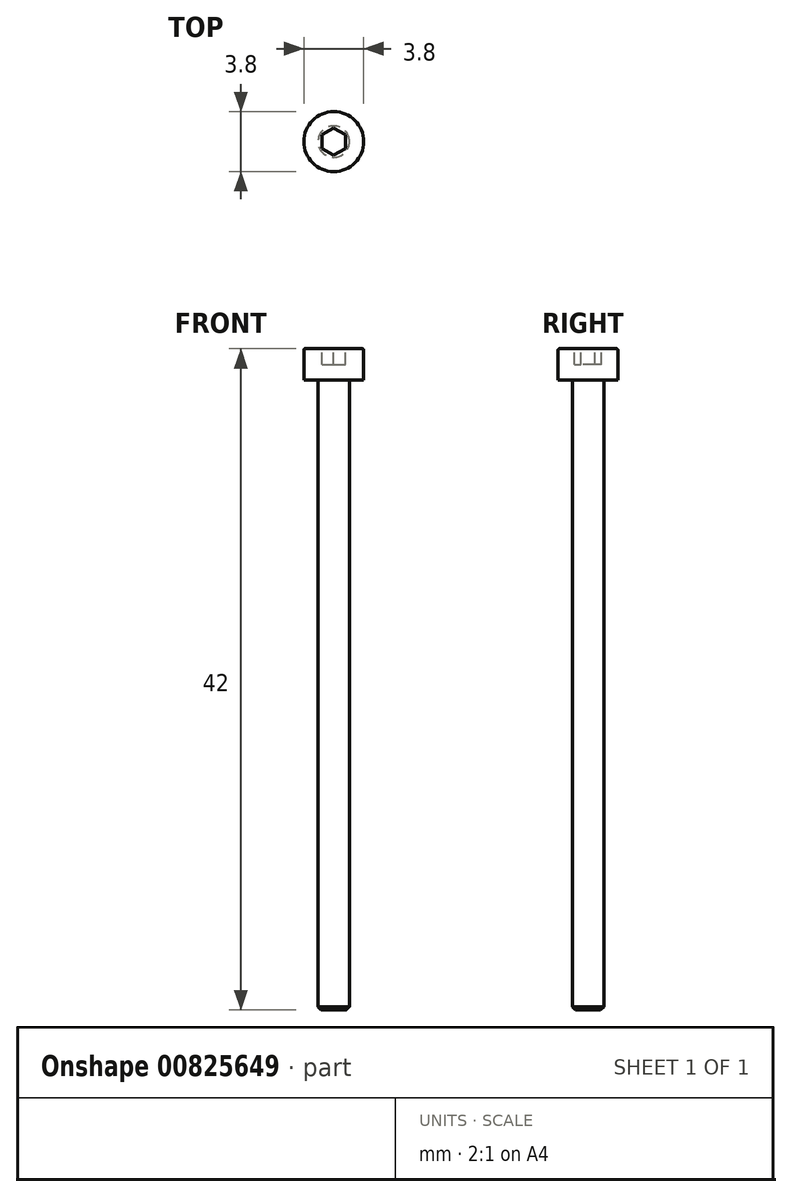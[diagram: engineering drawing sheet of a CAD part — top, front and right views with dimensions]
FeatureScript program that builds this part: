
annotation { "Feature Type Name" : "Feature", "Feature Type Description" : "" }
export const myFeature = defineFeature(function(context is Context, id is Id, definition is map)
    precondition{}
    {
        {
            assignVariable(context, id + "F0", {"name" : "Head_t", "anyValue" : 1});
        }
        {
            var Q0;
            Q0=qCreatedBy(makeId("Front.planeOp"),FACE);
            var sketch = newSketch(context, id + "F1", { "sketchPlane" : qUnion([Q0])});
            skLineSegment(sketch, "E0", {"start": v(0, 2) * mm, "end": v(1.8, 2) * mm});
            skLineSegment(sketch, "E1", {"start": v(1.9, 1.9) * mm, "end": v(1.9, 0) * mm});
            skLineSegment(sketch, "E2", {"start": v(1.9, 0) * mm, "end": v(0, 0) * mm});
            skLineSegment(sketch, "E3", {"start": v(0, 0) * mm, "end": v(0, 2) * mm});
            skPoint(sketch, "E4.orphan", {"position": v(0, -40) * mm});
            skPoint(sketch, "E5.visualSharp", {"position": v(1.9, 2) * mm});
            skArc(sketch, "E5.filletArc", {"start": v(1.9, 1.9) * mm, "mid": v(1.87, 1.97) * mm, "end": v(1.8, 2) * mm});
            skSolve(sketch);
        }
        {
            var Q0;
            Q0=makeQuery(id+"F1.imprint","IMPRINT",FACE,{"disambiguationData":[TD([[makeQuery(id+"F1.imprint","IMPRINT",EDGE,{"derivedFrom":sQuery(id+"F1.wireOp",EDGE,"E0")}),-1.0]])]});
            var Q1;
            Q1=sQuery(id+"F1.wireOp",EDGE,"E3");
            revolve(context, id + "F2", {"entities" : qUnion([Q0]), "axis" : qUnion([Q1]), "revolveType" : RevolveType.FULL});
        }
        {
            var Q0;
            Q0=makeQuery(id+"F2.opRevolve","SWEPT_FACE",FACE,{"disambiguationData":[OSD([sQuery(id+"F1.wireOp",EDGE,"E0")])]});
            var sketch = newSketch(context, id + "F3", { "sketchPlane" : qUnion([Q0])});
            skCircle(sketch, "E6.cCircle", {"center": v(0, 0) * mm, "radius": 0.75 * mm, "construction": true});
            skLineSegment(sketch, "E6.0", {"start": v(0.75, 0.43) * mm, "end": v(0.75, -0.43) * mm});
            skLineSegment(sketch, "E6.1", {"start": v(0.75, -0.43) * mm, "end": v(0, -0.87) * mm});
            skLineSegment(sketch, "E6.2", {"start": v(0, -0.87) * mm, "end": v(-0.75, -0.43) * mm});
            skLineSegment(sketch, "E6.3", {"start": v(-0.75, -0.43) * mm, "end": v(-0.75, 0.43) * mm});
            skLineSegment(sketch, "E6.4", {"start": v(-0.75, 0.43) * mm, "end": v(0, 0.87) * mm});
            skLineSegment(sketch, "E6.5", {"start": v(0, 0.87) * mm, "end": v(0.75, 0.43) * mm});
            skPoint(sketch, "E6.0.midPoint", {"position": v(0.75, 0) * mm});
            skSolve(sketch);
        }
        {
            var Q0;
            Q0=qSketchRegion(id+"F3",true);
            extrude(context, id + "F4", {"entities" : qUnion([Q0]), "operationType" : NewBodyOperationType.REMOVE, "oppositeDirection" : true, "depth" : (getVariable(context, 'Head_t')) * mm});
        }
        {
            var Q0;
            Q0=makeQuery(id+"F2.opRevolve","SWEPT_BODY",BODY,{"disambiguationData":[OSD([sQuery(id+"F1.wireOp",EDGE,"E0"),sQuery(id+"F1.wireOp",EDGE,"E1"),sQuery(id+"F1.wireOp",EDGE,"E2"),sQuery(id+"F1.wireOp",EDGE,"E3")])]});
            transform(context, id + "F5", {"entities" : qUnion([Q0]), "transformType" : TransformType.TRANSLATION_3D, "dx" : 0 * mm, "dy" : 0 * mm, "dz" : 0 * mm, "makeCopy" : true});
        }
        {
            var Q0;
            Q0=qCreatedBy(makeId("Front.planeOp"),FACE);
            var sketch = newSketch(context, id + "F6", { "sketchPlane" : qUnion([Q0])});
            skLineSegment(sketch, "E7.bottom", {"start": v(0, 0) * mm, "end": v(1, 0) * mm});
            skLineSegment(sketch, "E7.top", {"start": v(0, -8) * mm, "end": v(0.8, -8) * mm});
            skLineSegment(sketch, "E7.left", {"start": v(0, 0) * mm, "end": v(0, -8) * mm});
            skLineSegment(sketch, "E7.right", {"start": v(1, 0) * mm, "end": v(1, -7.8) * mm});
            skLineSegment(sketch, "E8", {"start": v(0.8, -8) * mm, "end": v(1, -7.8) * mm});
            skSolve(sketch);
        }
        {
            var Q0;
            Q0=qSketchRegion(id+"F6",true);
            var Q1;
            Q1=sQuery(id+"F6.wireOp",EDGE,"E7.left");
            revolve(context, id + "F7", {"operationType" : NewBodyOperationType.ADD, "entities" : qUnion([Q0]), "axis" : qUnion([Q1]), "revolveType" : RevolveType.FULL});
        }
        {
            var Q0;
            Q0=makeQuery(id+"F2.opRevolve","SWEPT_BODY",BODY,{"disambiguationData":[OSD([sQuery(id+"F1.wireOp",EDGE,"E0"),sQuery(id+"F1.wireOp",EDGE,"E1"),sQuery(id+"F1.wireOp",EDGE,"E2"),sQuery(id+"F1.wireOp",EDGE,"E3")])]});
            transform(context, id + "F8", {"entities" : qUnion([Q0]), "transformType" : TransformType.TRANSLATION_3D, "dx" : 0 * mm, "dy" : 0 * mm, "dz" : 0 * mm, "makeCopy" : true});
        }
        {
            var Q0;
            Q0=qCreatedBy(makeId("Front.planeOp"),FACE);
            var sketch = newSketch(context, id + "F9", { "sketchPlane" : qUnion([Q0])});
            skLineSegment(sketch, "E9.bottom", {"start": v(0, 0) * mm, "end": v(1, 0) * mm});
            skLineSegment(sketch, "E9.top", {"start": v(0, -10) * mm, "end": v(0.8, -10) * mm});
            skLineSegment(sketch, "E9.left", {"start": v(0, 0) * mm, "end": v(0, -10) * mm});
            skLineSegment(sketch, "E9.right", {"start": v(1, 0) * mm, "end": v(1, -9.8) * mm});
            skLineSegment(sketch, "E10", {"start": v(0.8, -10) * mm, "end": v(1, -9.8) * mm});
            skSolve(sketch);
        }
        {
            var Q0;
            Q0=qSketchRegion(id+"F9",true);
            var Q1;
            Q1=sQuery(id+"F9.wireOp",EDGE,"E9.left");
            revolve(context, id + "F10", {"operationType" : NewBodyOperationType.ADD, "entities" : qUnion([Q0]), "axis" : qUnion([Q1]), "revolveType" : RevolveType.FULL});
        }
        {
            var Q0;
            Q0=makeQuery(id+"F2.opRevolve","SWEPT_BODY",BODY,{"disambiguationData":[OSD([sQuery(id+"F1.wireOp",EDGE,"E0"),sQuery(id+"F1.wireOp",EDGE,"E1"),sQuery(id+"F1.wireOp",EDGE,"E2"),sQuery(id+"F1.wireOp",EDGE,"E3"),sQuery(id+"F1.wireOp",EDGE,"E5.filletArc")])]});
            transform(context, id + "F11", {"entities" : qUnion([Q0]), "transformType" : TransformType.TRANSLATION_3D, "dx" : 0 * mm, "dy" : 0 * mm, "dz" : 0 * mm, "makeCopy" : true});
        }
        {
            var Q0;
            Q0=qCreatedBy(makeId("Front.planeOp"),FACE);
            var sketch = newSketch(context, id + "F12", { "sketchPlane" : qUnion([Q0])});
            skLineSegment(sketch, "E11.bottom", {"start": v(0, 0) * mm, "end": v(1, 0) * mm});
            skLineSegment(sketch, "E11.top", {"start": v(0, -30) * mm, "end": v(0.8, -30) * mm});
            skLineSegment(sketch, "E11.left", {"start": v(0, 0) * mm, "end": v(0, -30) * mm});
            skLineSegment(sketch, "E11.right", {"start": v(1, 0) * mm, "end": v(1, -29.8) * mm});
            skLineSegment(sketch, "E12", {"start": v(0.8, -30) * mm, "end": v(1, -29.8) * mm});
            skSolve(sketch);
        }
        {
            var Q0;
            Q0=qSketchRegion(id+"F12",true);
            var Q1;
            Q1=sQuery(id+"F12.wireOp",EDGE,"E11.left");
            revolve(context, id + "F13", {"operationType" : NewBodyOperationType.ADD, "entities" : qUnion([Q0]), "axis" : qUnion([Q1]), "revolveType" : RevolveType.FULL});
        }
        {
            var Q0;
            Q0=makeQuery(id+"F2.opRevolve","SWEPT_BODY",BODY,{"disambiguationData":[OSD([sQuery(id+"F1.wireOp",EDGE,"E0"),sQuery(id+"F1.wireOp",EDGE,"E1"),sQuery(id+"F1.wireOp",EDGE,"E2"),sQuery(id+"F1.wireOp",EDGE,"E3"),sQuery(id+"F1.wireOp",EDGE,"E5.filletArc")])]});
            transform(context, id + "F14", {"entities" : qUnion([Q0]), "transformType" : TransformType.TRANSLATION_3D, "dx" : 0 * mm, "dy" : 0 * mm, "dz" : 0 * mm, "makeCopy" : true});
        }
        {
            var Q0;
            Q0=qCreatedBy(makeId("Front.planeOp"),FACE);
            var sketch = newSketch(context, id + "F15", { "sketchPlane" : qUnion([Q0])});
            skLineSegment(sketch, "E13.bottom", {"start": v(0, 0) * mm, "end": v(1, 0) * mm});
            skLineSegment(sketch, "E13.top", {"start": v(0, -40) * mm, "end": v(0.8, -40) * mm});
            skLineSegment(sketch, "E13.left", {"start": v(0, 0) * mm, "end": v(0, -40) * mm});
            skLineSegment(sketch, "E13.right", {"start": v(1, 0) * mm, "end": v(1, -39.8) * mm});
            skLineSegment(sketch, "E14", {"start": v(0.8, -40) * mm, "end": v(1, -39.8) * mm});
            skLineSegment(sketch, "E15", {"start": v(0.98, -22) * mm, "end": v(2, -22) * mm});
            skLineSegment(sketch, "E16", {"start": v(2, -22) * mm, "end": v(2, -22.59) * mm});
            skLineSegment(sketch, "E17", {"start": v(2, -22.59) * mm, "end": v(0.98, -22) * mm});
            skSolve(sketch);
        }
        {
            var Q0;
            {var subQ1=sQuery(id+"F15.wireOp",EDGE,"E13.bottom");Q0=makeQuery(id+"F15.imprint","IMPRINT",FACE,{"disambiguationData":[TD([[makeQuery(id+"F15.imprint","IMPRINT",EDGE,{"derivedFrom":subQ1}),-1.0]])]});}
            var Q1;
            Q1=sQuery(id+"F15.wireOp",EDGE,"E13.left");
            revolve(context, id + "F16", {"operationType" : NewBodyOperationType.ADD, "entities" : qUnion([Q0]), "axis" : qUnion([Q1]), "revolveType" : RevolveType.FULL});
        }
        {
            var Q0;
            Q0=makeQuery(id+"F2.opRevolve","SWEPT_BODY",BODY,{"disambiguationData":[OSD([sQuery(id+"F1.wireOp",EDGE,"E0"),sQuery(id+"F1.wireOp",EDGE,"E1"),sQuery(id+"F1.wireOp",EDGE,"E2"),sQuery(id+"F1.wireOp",EDGE,"E3"),sQuery(id+"F1.wireOp",EDGE,"E5.filletArc")])]});
            transform(context, id + "F17", {"entities" : qUnion([Q0]), "transformType" : TransformType.TRANSLATION_3D, "dx" : 0 * mm, "dy" : 0 * mm, "dz" : 0 * mm, "makeCopy" : true});
        }
        {
            var Q0;
            Q0=qCreatedBy(makeId("Front.planeOp"),FACE);
            var sketch = newSketch(context, id + "F18", { "sketchPlane" : qUnion([Q0])});
            skLineSegment(sketch, "E18.bottom", {"start": v(0, 0) * mm, "end": v(1, 0) * mm});
            skLineSegment(sketch, "E18.top", {"start": v(0, -6) * mm, "end": v(0.8, -6) * mm});
            skLineSegment(sketch, "E18.left", {"start": v(0, 0) * mm, "end": v(0, -6) * mm});
            skLineSegment(sketch, "E18.right", {"start": v(1, 0) * mm, "end": v(1, -5.8) * mm});
            skLineSegment(sketch, "E19", {"start": v(0.8, -6) * mm, "end": v(1, -5.8) * mm});
            skSolve(sketch);
        }
        {
            var Q0;
            Q0=qSketchRegion(id+"F18",true);
            var Q1;
            Q1=sQuery(id+"F18.wireOp",EDGE,"E18.left");
            revolve(context, id + "F19", {"operationType" : NewBodyOperationType.ADD, "entities" : qUnion([Q0]), "axis" : qUnion([Q1]), "revolveType" : RevolveType.FULL});
        }
        {
            var Q0;
            Q0=makeQuery(id+"F2.opRevolve","SWEPT_BODY",BODY,{"disambiguationData":[OSD([sQuery(id+"F1.wireOp",EDGE,"E0"),sQuery(id+"F1.wireOp",EDGE,"E1"),sQuery(id+"F1.wireOp",EDGE,"E2"),sQuery(id+"F1.wireOp",EDGE,"E3"),sQuery(id+"F1.wireOp",EDGE,"E5.filletArc")])]});
            transform(context, id + "F20", {"entities" : qUnion([Q0]), "transformType" : TransformType.TRANSLATION_3D, "dx" : 0 * mm, "dy" : 0 * mm, "dz" : 0 * mm, "makeCopy" : true});
        }
        {
            var Q0;
            Q0=qCreatedBy(makeId("Front.planeOp"),FACE);
            var sketch = newSketch(context, id + "F21", { "sketchPlane" : qUnion([Q0])});
            skLineSegment(sketch, "E20", {"start": v(0, 0) * mm, "end": v(1, 0) * mm});
            skLineSegment(sketch, "E21", {"start": v(1, 0) * mm, "end": v(1, -15.8) * mm});
            skLineSegment(sketch, "E22", {"start": v(1, -15.8) * mm, "end": v(0.8, -16) * mm});
            skLineSegment(sketch, "E23", {"start": v(0.8, -16) * mm, "end": v(0, -16) * mm});
            skLineSegment(sketch, "E24", {"start": v(0, -16) * mm, "end": v(0, 0) * mm});
            skSolve(sketch);
        }
        {
            var Q0;
            Q0=qSketchRegion(id+"F21",true);
            var Q1;
            Q1=sQuery(id+"F21.wireOp",EDGE,"E24");
            revolve(context, id + "F22", {"operationType" : NewBodyOperationType.ADD, "surfaceOperationType" : NewSurfaceOperationType.NEW, "entities" : qUnion([Q0]), "axis" : qUnion([Q1]), "revolveType" : RevolveType.FULL});
        }
        {
            var Q0;
            Q0=makeQuery(id+"F2.opRevolve","SWEPT_BODY",BODY,{"disambiguationData":[OSD([sQuery(id+"F1.wireOp",EDGE,"E0"),sQuery(id+"F1.wireOp",EDGE,"E1"),sQuery(id+"F1.wireOp",EDGE,"E2"),sQuery(id+"F1.wireOp",EDGE,"E3"),sQuery(id+"F1.wireOp",EDGE,"E5.filletArc")])]});
            transform(context, id + "F23", {"entities" : qUnion([Q0]), "transformType" : TransformType.TRANSLATION_3D, "dx" : 0 * mm, "dy" : 0 * mm, "dz" : 0 * mm, "makeCopy" : true});
        }
        {
            var Q0;
            Q0=qCreatedBy(makeId("Front.planeOp"),FACE);
            var sketch = newSketch(context, id + "F24", { "sketchPlane" : qUnion([Q0])});
            skLineSegment(sketch, "E25", {"start": v(0, 0) * mm, "end": v(1, 0) * mm});
            skLineSegment(sketch, "E26", {"start": v(1, 0) * mm, "end": v(1, -11.8) * mm});
            skLineSegment(sketch, "E27", {"start": v(1, -11.8) * mm, "end": v(0.8, -12) * mm});
            skLineSegment(sketch, "E28", {"start": v(0.8, -12) * mm, "end": v(0, -12) * mm});
            skLineSegment(sketch, "E29", {"start": v(0, -12) * mm, "end": v(0, 0) * mm});
            skSolve(sketch);
        }
        {
            var Q0;
            Q0=qSketchRegion(id+"F24",true);
            var Q1;
            Q1=sQuery(id+"F24.wireOp",EDGE,"E29");
            revolve(context, id + "F25", {"operationType" : NewBodyOperationType.ADD, "surfaceOperationType" : NewSurfaceOperationType.NEW, "entities" : qUnion([Q0]), "axis" : qUnion([Q1]), "revolveType" : RevolveType.FULL});
        }
        {
            var Q0;
            Q0=makeQuery(id+"F2.opRevolve","SWEPT_BODY",BODY,{"disambiguationData":[OSD([sQuery(id+"F1.wireOp",EDGE,"E0"),sQuery(id+"F1.wireOp",EDGE,"E1"),sQuery(id+"F1.wireOp",EDGE,"E2"),sQuery(id+"F1.wireOp",EDGE,"E3"),sQuery(id+"F1.wireOp",EDGE,"E5.filletArc")])]});
            transform(context, id + "F26", {"entities" : qUnion([Q0]), "transformType" : TransformType.TRANSLATION_3D, "dx" : 0 * mm, "dy" : 0 * mm, "dz" : 0 * mm, "makeCopy" : true});
        }
        {
            var Q0;
            Q0=qCreatedBy(makeId("Front.planeOp"),FACE);
            var sketch = newSketch(context, id + "F27", { "sketchPlane" : qUnion([Q0])});
            skLineSegment(sketch, "E30", {"start": v(0, 0) * mm, "end": v(1, 0) * mm});
            skLineSegment(sketch, "E31", {"start": v(1, 0) * mm, "end": v(1, -17.8) * mm});
            skLineSegment(sketch, "E32", {"start": v(1, -17.8) * mm, "end": v(0.8, -18) * mm});
            skLineSegment(sketch, "E33", {"start": v(0.8, -18) * mm, "end": v(0, -18) * mm});
            skLineSegment(sketch, "E34", {"start": v(0, -18) * mm, "end": v(0, 0) * mm});
            skSolve(sketch);
        }
        {
            var Q0;
            Q0=qSketchRegion(id+"F27",true);
            var Q1;
            Q1=sQuery(id+"F27.wireOp",EDGE,"E34");
            revolve(context, id + "F28", {"operationType" : NewBodyOperationType.ADD, "surfaceOperationType" : NewSurfaceOperationType.NEW, "entities" : qUnion([Q0]), "axis" : qUnion([Q1]), "revolveType" : RevolveType.FULL});
        }
    });
